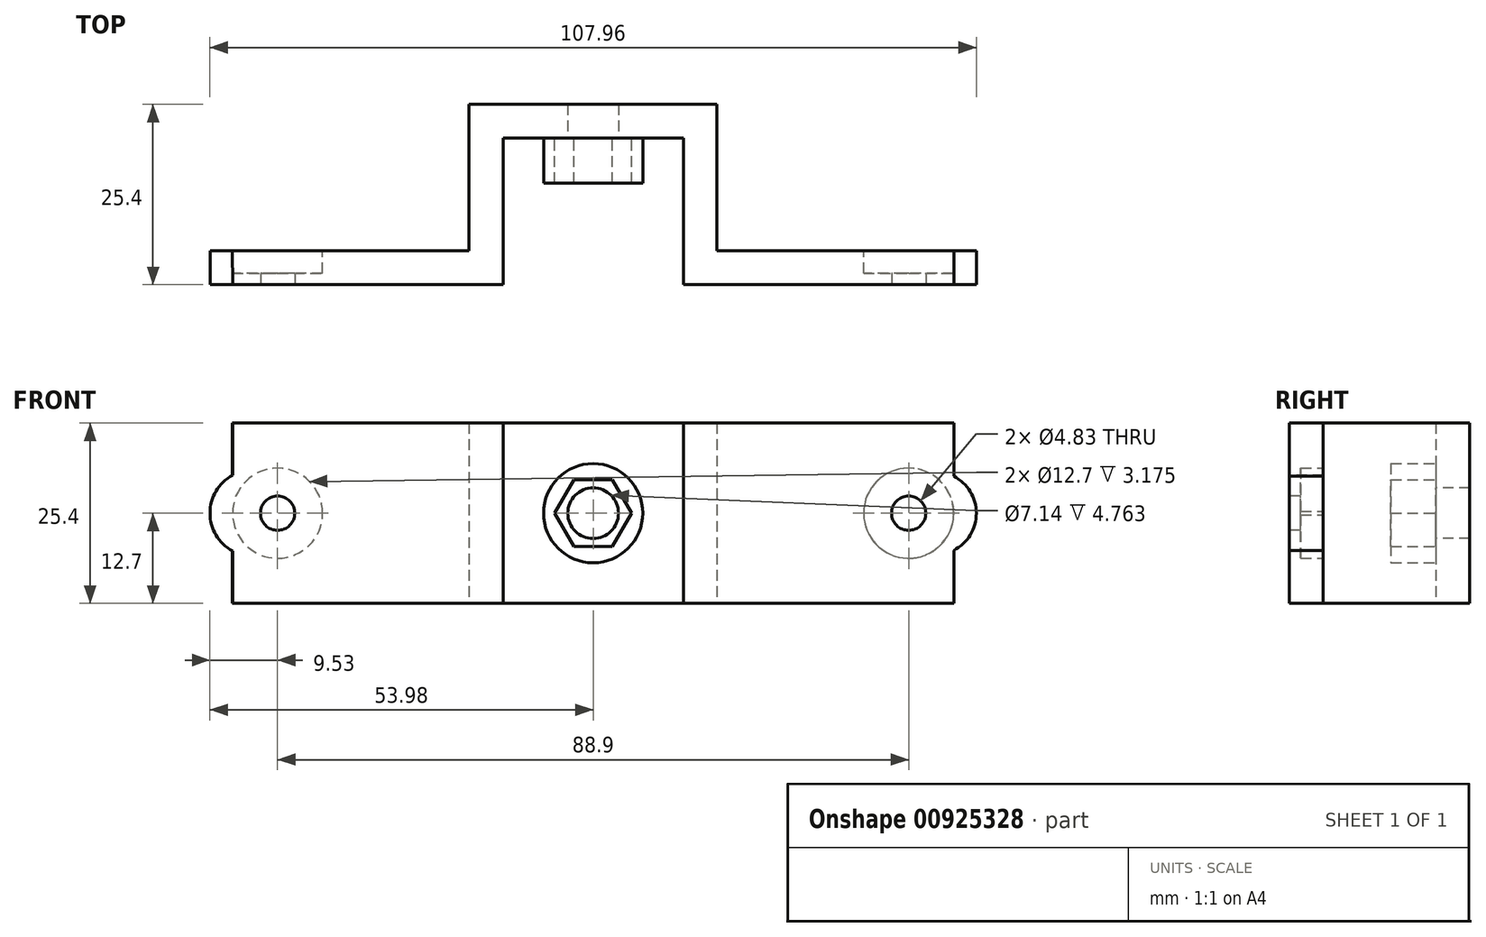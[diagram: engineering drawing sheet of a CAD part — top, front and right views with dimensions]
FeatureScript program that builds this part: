
annotation { "Feature Type Name" : "Feature", "Feature Type Description" : "" }
export const myFeature = defineFeature(function(context is Context, id is Id, definition is map)
    precondition{}
    {
        {
            var Q0;
            Q0=qCreatedBy(makeId("Top.planeOp"),FACE);
            var sketch = newSketch(context, id + "F0", { "sketchPlane" : qUnion([Q0])});
            skLineSegment(sketch, "E0", {"start": v(-50.8, -20.64) * mm, "end": v(-12.7, -20.64) * mm});
            skLineSegment(sketch, "E1", {"start": v(-12.7, -20.64) * mm, "end": v(-12.7, 0) * mm});
            skLineSegment(sketch, "E2", {"start": v(-12.7, 0) * mm, "end": v(12.7, 0) * mm});
            skLineSegment(sketch, "E3", {"start": v(12.7, 0) * mm, "end": v(12.7, -20.64) * mm});
            skLineSegment(sketch, "E4", {"start": v(12.7, -20.64) * mm, "end": v(50.8, -20.64) * mm});
            skLineSegment(sketch, "E5", {"start": v(50.8, -20.64) * mm, "end": v(50.8, -15.87) * mm});
            skLineSegment(sketch, "E6", {"start": v(50.8, -15.87) * mm, "end": v(17.45, -15.88) * mm});
            skLineSegment(sketch, "E7", {"start": v(17.45, -15.87) * mm, "end": v(17.45, 4.76) * mm});
            skLineSegment(sketch, "E8", {"start": v(17.45, 4.76) * mm, "end": v(-17.48, 4.76) * mm});
            skLineSegment(sketch, "E9", {"start": v(-17.48, 4.76) * mm, "end": v(-17.48, -15.87) * mm});
            skLineSegment(sketch, "E10", {"start": v(-17.48, -15.88) * mm, "end": v(-50.83, -15.88) * mm});
            skLineSegment(sketch, "E11", {"start": v(-50.83, -15.87) * mm, "end": v(-50.8, -20.64) * mm});
            skSolve(sketch);
        }
        {
            var Q0;
            Q0 = qSketchRegion(id + "F0", true);
            extrude(context, id + "F1", {"entities" : qUnion([Q0]), "depth" : 25.4 * mm, "offsetDistance" : 25.4 * mm});
        }
        {
            var Q0;
            Q0=makeQuery(id+"F1.opExtrude","SWEPT_FACE",FACE,{"disambiguationData":[OSD([sQuery(id+"F0.wireOp",EDGE,"E2")])]});
            var sketch = newSketch(context, id + "F2", { "sketchPlane" : qUnion([Q0])});
            skCircle(sketch, "E12", {"center": v(0, 12.7) * mm, "radius": 3.57 * mm});
            skSolve(sketch);
        }
        {
            var Q0;
            Q0 = qSketchRegion(id + "F2", true);
            extrude(context, id + "F3", {"entities" : qUnion([Q0]), "operationType" : NewBodyOperationType.REMOVE, "oppositeDirection" : true, "depth" : 4.76 * mm, "offsetDistance" : 25.4 * mm});
        }
        {
            var Q0;
            Q0=makeQuery(id+"F1.opExtrude","SWEPT_FACE",FACE,{"disambiguationData":[OSD([sQuery(id+"F0.wireOp",EDGE,"E2")])]});
            var sketch = newSketch(context, id + "F4", { "sketchPlane" : qUnion([Q0])});
            skCircle(sketch, "E13.cCircle", {"center": v(0, 12.7) * mm, "radius": 4.7 * mm, "construction": true});
            skLineSegment(sketch, "E13.0", {"start": v(-5.43, 12.7) * mm, "end": v(-2.71, 17.4) * mm});
            skLineSegment(sketch, "E13.1", {"start": v(-2.71, 17.4) * mm, "end": v(2.71, 17.4) * mm});
            skLineSegment(sketch, "E13.2", {"start": v(2.71, 17.4) * mm, "end": v(5.43, 12.7) * mm});
            skLineSegment(sketch, "E13.3", {"start": v(5.43, 12.7) * mm, "end": v(2.71, 8) * mm});
            skLineSegment(sketch, "E13.4", {"start": v(2.71, 8) * mm, "end": v(-2.71, 8) * mm});
            skLineSegment(sketch, "E13.5", {"start": v(-2.71, 8) * mm, "end": v(-5.43, 12.7) * mm});
            skPoint(sketch, "E13.0.midPoint", {"position": v(-4.07, 15.05) * mm});
            skCircle(sketch, "E14", {"center": v(0, 12.7) * mm, "radius": 6.99 * mm});
            skSolve(sketch);
        }
        {
            var Q0;
            Q0 = qSketchRegion(id + "F4", true);
            extrude(context, id + "F5", {"entities" : qUnion([Q0]), "operationType" : NewBodyOperationType.ADD, "depth" : 6.35 * mm, "offsetDistance" : 25.4 * mm});
        }
        {
            var Q0;
            Q0=makeQuery(id+"F1.opExtrude","SWEPT_FACE",FACE,{"disambiguationData":[OSD([sQuery(id+"F0.wireOp",EDGE,"E4")])]});
            var sketch = newSketch(context, id + "F6", { "sketchPlane" : qUnion([Q0])});
            skCircle(sketch, "E15", {"center": v(-44.45, 12.7) * mm, "radius": 2.41 * mm});
            skCircle(sketch, "E16", {"center": v(44.45, 12.7) * mm, "radius": 2.41 * mm});
            skSolve(sketch);
        }
        {
            var Q0;
            Q0 = qSketchRegion(id + "F6", true);
            extrude(context, id + "F7", {"entities" : qUnion([Q0]), "operationType" : NewBodyOperationType.REMOVE, "oppositeDirection" : true, "depth" : 4.76 * mm, "offsetDistance" : 25.4 * mm});
        }
        {
            var Q0;
            Q0=makeQuery(id+"F1.opExtrude","SWEPT_FACE",FACE,{"disambiguationData":[OSD([sQuery(id+"F0.wireOp",EDGE,"E10")])]});
            var sketch = newSketch(context, id + "F8", { "sketchPlane" : qUnion([Q0])});
            skCircle(sketch, "E17", {"center": v(44.45, 12.7) * mm, "radius": 2.41 * mm});
            skCircle(sketch, "E18", {"center": v(-44.45, 12.7) * mm, "radius": 2.41 * mm});
            skCircle(sketch, "E19", {"center": v(44.45, 12.7) * mm, "radius": 6.35 * mm});
            skCircle(sketch, "E20", {"center": v(-44.45, 12.7) * mm, "radius": 6.35 * mm});
            skSolve(sketch);
        }
        {
            var Q0;
            Q0=makeQuery(id+"F1.opExtrude","SWEPT_FACE",FACE,{"disambiguationData":[OSD([sQuery(id+"F0.wireOp",EDGE,"E0")])]});
            var sketch = newSketch(context, id + "F9", { "sketchPlane" : qUnion([Q0])});
            skArc(sketch, "E21", {"start": v(-50.8, 18.05) * mm, "mid": v(-53.98, 12.7) * mm, "end": v(-50.8, 7.36) * mm});
            skLineSegment(sketch, "E22", {"start": v(-50.8, 18.05) * mm, "end": v(-50.8, 7.36) * mm});
            skPoint(sketch, "E23.orphan", {"position": v(-47.89, 18.8) * mm});
            skPoint(sketch, "E24.orphan", {"position": v(-47.89, 6.62) * mm});
            skArc(sketch, "E25", {"start": v(50.8, 7.46) * mm, "mid": v(53.98, 12.69) * mm, "end": v(50.8, 17.91) * mm});
            skLineSegment(sketch, "E26", {"start": v(50.8, 17.91) * mm, "end": v(50.8, 7.46) * mm});
            skPoint(sketch, "E27.orphan", {"position": v(48.1, 18.57) * mm});
            skPoint(sketch, "E28.orphan", {"position": v(48.1, 6.8) * mm});
            skSolve(sketch);
        }
        {
            var Q0;
            Q0 = qSketchRegion(id + "F9", true);
            extrude(context, id + "F10", {"entities" : qUnion([Q0]), "operationType" : NewBodyOperationType.ADD, "oppositeDirection" : true, "depth" : 4.76 * mm, "offsetDistance" : 25.4 * mm});
        }
        {
            var Q0;
            Q0 = qSketchRegion(id + "F8", true);
            extrude(context, id + "F11", {"entities" : qUnion([Q0]), "operationType" : NewBodyOperationType.REMOVE, "oppositeDirection" : true, "depth" : 3.17 * mm, "offsetDistance" : 25.4 * mm});
        }
        {
            var Q0;
            Q0 = qSketchRegion(id + "F9", true);
            extrude(context, id + "F12", {"entities" : qUnion([Q0]), "operationType" : NewBodyOperationType.ADD, "oppositeDirection" : true, "depth" : 4.75 * mm, "offsetDistance" : 25.4 * mm});
        }
    });
